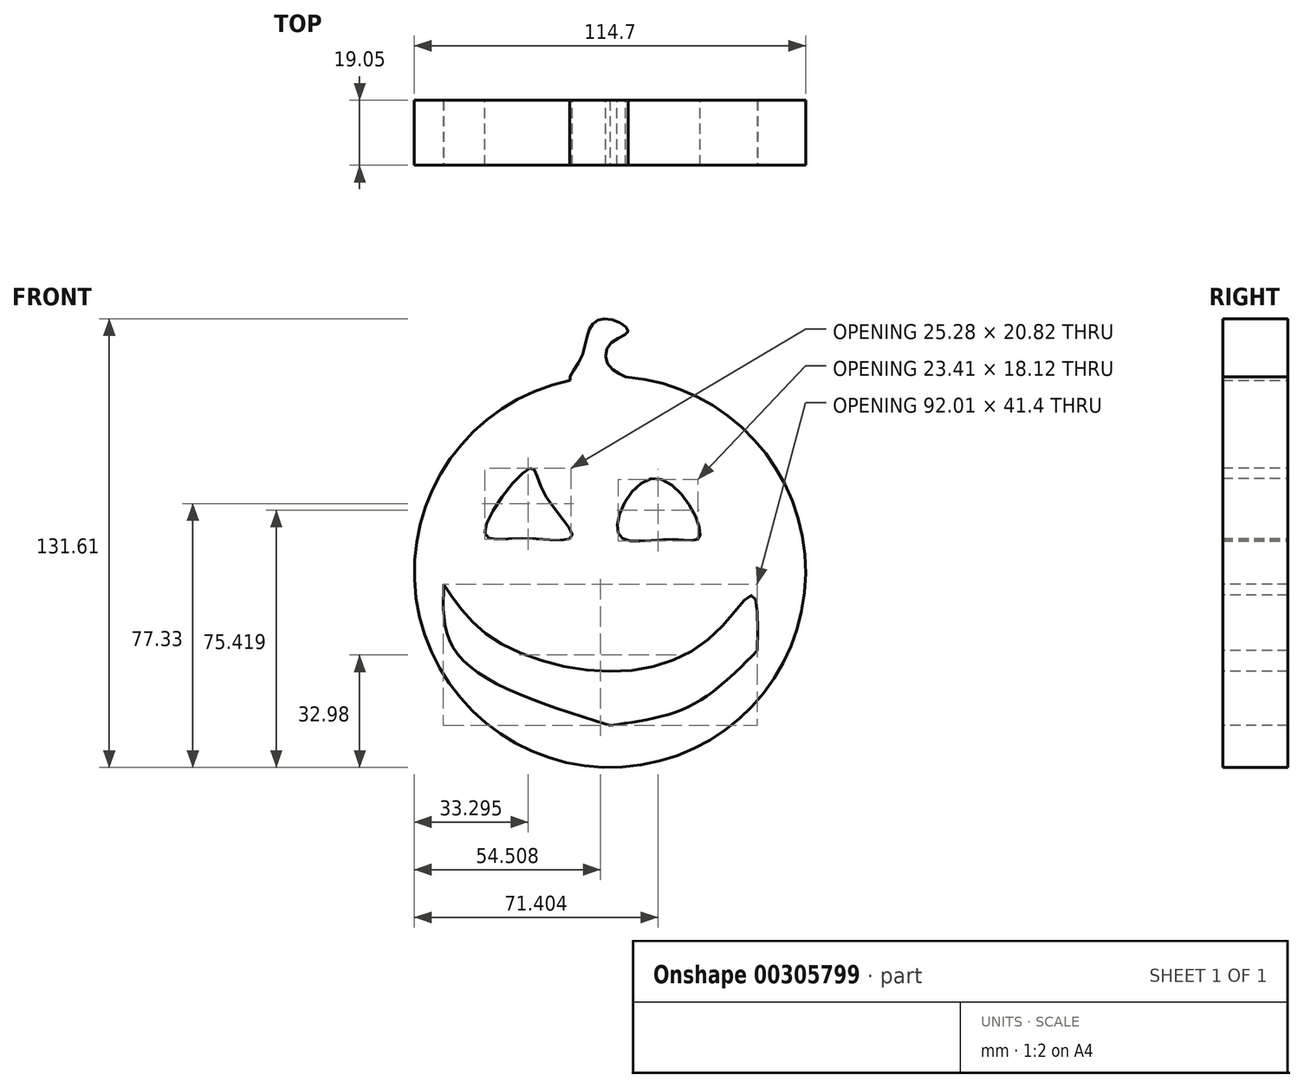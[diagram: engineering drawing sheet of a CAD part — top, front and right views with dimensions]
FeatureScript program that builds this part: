
annotation { "Feature Type Name" : "Feature", "Feature Type Description" : "" }
export const myFeature = defineFeature(function(context is Context, id is Id, definition is map)
    precondition{}
    {
        {
            var Q0;
            Q0=qCreatedBy(makeId("Front.planeOp"),FACE);
            var sketch = newSketch(context, id + "F0", { "sketchPlane" : qUnion([Q0])});
            skCircle(sketch, "E0", {"center": v(0, 0) * mm, "radius": 57.35 * mm});
            skSolve(sketch);
        }
        {
            var Q0;
            Q0=makeQuery(id+"F0.imprint","IMPRINT",FACE,{"disambiguationData":[TD([[makeQuery(id+"F0.imprint","IMPRINT",EDGE,{"derivedFrom":sQuery(id+"F0.wireOp",EDGE,"E0")}),1.0]])]});
            extrude(context, id + "F1", {"entities" : qUnion([Q0]), "depth" : 19.05 * mm});
        }
        {
            var Q0;
            Q0=makeQuery(id+"F1.opExtrude","CAP_FACE",FACE,{"disambiguationData":[OSD([sQuery(id+"F0.wireOp",EDGE,"E0")])],"isStart":false});
            var sketch = newSketch(context, id + "F2", { "sketchPlane" : qUnion([Q0])});
            skFitSpline(sketch, "E1", {"points": [v(-23.49, 30.39) * mm, v(-36.7, 11.6) * mm, v(-25.84, 9.84) * mm, v(-11.16, 10.42) * mm, v(-19.97, 24.22) * mm, v(-23.49, 30.39) * mm]});
            skFitSpline(sketch, "E2", {"points": [v(2.35, 11.3) * mm, v(13.21, 27.45) * mm, v(26.43, 10.72) * mm, v(17.62, 9.54) * mm, v(2.35, 11.3) * mm]});
            skSolve(sketch);
        }
        {
            var Q0;
            Q0 = qSketchRegion(id + "F2", true);
            extrude(context, id + "F3", {"entities" : qUnion([Q0]), "operationType" : NewBodyOperationType.REMOVE, "oppositeDirection" : true, "depth" : 25.4 * mm});
        }
        {
            var Q0;
            Q0=makeQuery(id+"F1.opExtrude","CAP_FACE",FACE,{"disambiguationData":[OSD([sQuery(id+"F0.wireOp",EDGE,"E0")])],"isStart":false});
            var sketch = newSketch(context, id + "F4", { "sketchPlane" : qUnion([Q0])});
            skFitSpline(sketch, "E3", {"points": [v(-48.74, -3.67) * mm, v(-35.23, -18.94) * mm, v(0, -29.21) * mm, v(30.54, -18.35) * mm, v(41.7, -6.9) * mm, v(43.16, -23.05) * mm], "startDerivative": vector(57, -87.28) * mm, "endDerivative": vector(-3.56, -141.98) * mm});
            skFitSpline(sketch, "E4", {"points": [v(-48.74, -3.67) * mm, v(-44.63, -24.22) * mm, v(0, -45.07) * mm], "startDerivative": vector(-2.09, -55.54) * mm, "endDerivative": vector(92.9, -29.11) * mm});
            skFitSpline(sketch, "E5", {"points": [v(0, -45.07) * mm, v(23.78, -39.2) * mm, v(43.16, -23.05) * mm], "startDerivative": vector(50.26, 6.81) * mm, "endDerivative": vector(36.1, 37.16) * mm});
            skSolve(sketch);
        }
        {
            var Q0;
            Q0=makeQuery(id+"F4.imprint","IMPRINT",FACE,{"disambiguationData":[TD([[makeQuery(id+"F4.imprint","IMPRINT",EDGE,{"derivedFrom":sQuery(id+"F4.wireOp",EDGE,"E3")}),-1.0]])]});
            extrude(context, id + "F5", {"entities" : qUnion([Q0]), "operationType" : NewBodyOperationType.REMOVE, "oppositeDirection" : true, "depth" : 25.4 * mm});
        }
        {
            var Q0;
            Q0=qCreatedBy(makeId("Front.planeOp"),FACE);
            var sketch = newSketch(context, id + "F6", { "sketchPlane" : qUnion([Q0])});
            skFitSpline(sketch, "E6", {"points": [v(-11.74, 56.23) * mm, v(0, 56.81) * mm, v(5.29, 56.81) * mm, v(0, 60.04) * mm, v(0, 66.8) * mm, v(5.29, 70.61) * mm, v(0, 74.14) * mm, v(-5.58, 72.08) * mm, v(-8.51, 62.69) * mm, v(-11.74, 56.23) * mm]});
            skSolve(sketch);
        }
        {
            var Q0;
            Q0 = qSketchRegion(id + "F6", true);
            extrude(context, id + "F7", {"entities" : qUnion([Q0]), "operationType" : NewBodyOperationType.ADD, "depth" : 19.05 * mm});
        }
    });
